# Revit family: ShowerHead-Strato-2F-Built-in-Vitra-OtherSeries-A45712
name_source: partatom
category: Plumbing Fixtures
revit_build: Autodesk Revit 2017 (Build: 20160225_1515(x64)
units: mm (PartAtom-declared; Revit-internal decimal feet)

## family parameters
Cut with Voids When Loaded = No
Host = Face
OmniClass Number = 23.45.00.00
OmniClass Title = Sanitary, Laundry, and Cleaning Equipment
Part Type = Normal
Room Calculation Point = No
Round Connector Dimension = Use Diameter
Shared = Yes

## types (1)
- ShowerHead-Strato-2F-Built-in-Vitra-OtherSeries-A45712
    Article No. (default) = A45712
    BIMobject category = Bath/Shower Mixer
    Brand = VitrA
    CW Connection = Yes
    Coating Material = Chrome
    Color = Chrome
    Connection Diameter (mm) = 20 mm  [stored 0.0656168 ft]
    Default Elevation = 0 mm  [stored 0 ft]
    Description = Strato 2F Built-in Showerhead
    Design country = Turkey
    HW Connection = Yes
    IFC Classification = Sanitary Terminal
    Main Material = Metal
    Manufacturer = Vitra
    Manufacturer name = Vitra
    Masterformat 2014 Code = 22 41 23
    Masterformat 2014 Description = Residential Showers
    Model = A45712
    Mounting type = Wall Mounted
    NBS Referans Code = 35-06-81
    NBS Referans Description = Shower Heads
    Nominal Depth (mm) = 583 mm
    Nominal Height (mm) = 120 mm  [stored 0.393701 ft]
    Nominal Width (mm) = 245 mm
    Number Of Connections = 1
    OmniClass Code = 23-31 17 19
    OmniClass Description = Shower Head Fixtures
    Product SKU = A45712
    Product Type = Showerhead
    Product certification = https://www.vitraglobal.com
    Product family = StratoSeries
    Product group = Showers Head
    Product url = https://www.vitra-india.com
    Technical description = https://www.vitra-india.com
    URL = https://vitraglobal.com
    Uniclass 1.4 Code = L7214
    Uniclass 1.4 Description = Showers
    Uniclass 2.0 Code = PR-35-06-81
    Uniclass 2.0 Description = Shower Heads
    Uniclass 2015 Code = Pr_40_20_87_76
    Uniclass 2015 Name = Shower heads
    Uniformat II Code = D2010
    Uniformat II Description = Plumbing Fixtures
    Vent Connection = No
    Warranty Period (Year) = 5 Years
    Waste Connection = No
    Weight Net (kg) = 1.8
    Youtube = https://www.youtube.com

note: [stored X ft] marks values corroborated as IEEE doubles in the binary element streams (Revit-internal decimal feet)

## geometry (parser evidence)
native form markers: Sweep x3
no freeform markers — native parametric forms only
